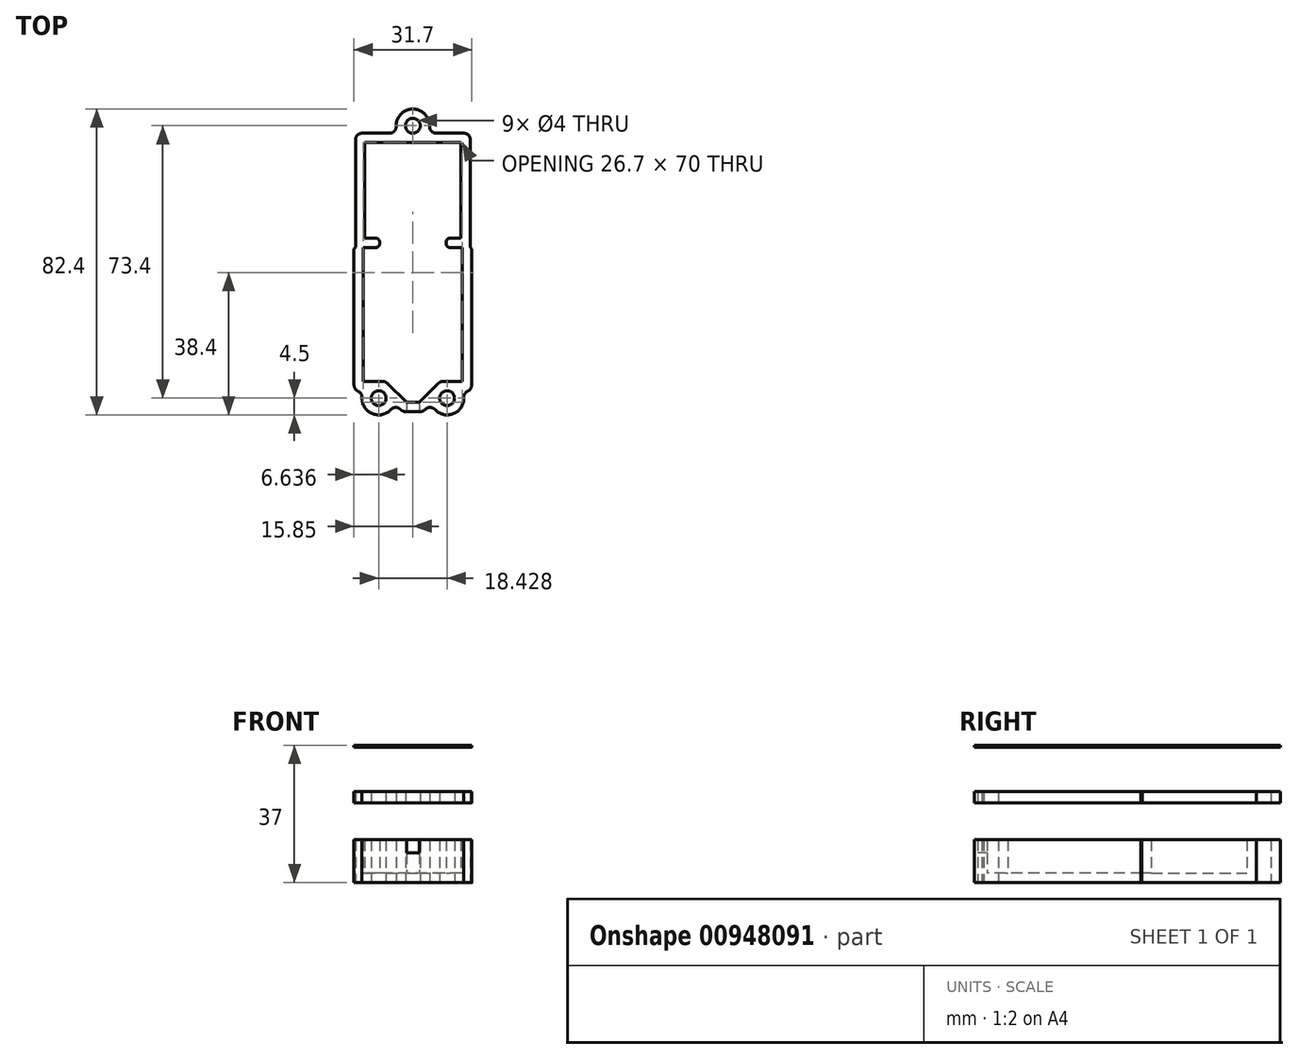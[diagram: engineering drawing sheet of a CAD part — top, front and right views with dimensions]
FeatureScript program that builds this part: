
annotation { "Feature Type Name" : "Feature", "Feature Type Description" : "" }
export const myFeature = defineFeature(function(context is Context, id is Id, definition is map)
    precondition{}
    {
        {
            var Q0;
            Q0=qCreatedBy(makeId("Top.planeOp"),FACE);
            var sketch = newSketch(context, id + "F0", { "sketchPlane" : qUnion([Q0])});
            skLineSegment(sketch, "E0.bottom", {"start": v(12.95, -12.9) * mm, "end": v(8.95, -12.9) * mm});
            skLineSegment(sketch, "E0.top", {"start": v(12.95, 12.9) * mm, "end": v(-12.95, 12.9) * mm});
            skLineSegment(sketch, "E0.left", {"start": v(12.95, -12.9) * mm, "end": v(12.95, 12.9) * mm});
            skLineSegment(sketch, "E0.right", {"start": v(-12.95, -12.9) * mm, "end": v(-12.95, 12.9) * mm});
            skPoint(sketch, "E0.middle", {"position": v(0, 0) * mm});
            skLineSegment(sketch, "E1.bottom", {"start": v(15.45, -15.4) * mm, "end": v(8.95, -15.4) * mm});
            skLineSegment(sketch, "E1.top", {"start": v(15.45, 15.4) * mm, "end": v(4.03, 15.4) * mm});
            skLineSegment(sketch, "E1.left", {"start": v(15.45, -15.4) * mm, "end": v(15.45, 15.4) * mm});
            skLineSegment(sketch, "E1.right", {"start": v(-15.45, -15.4) * mm, "end": v(-15.45, 15.4) * mm});
            skArc(sketch, "E2", {"start": v(4.03, 15.4) * mm, "mid": v(0, 21.9) * mm, "end": v(-4.03, 15.4) * mm});
            skCircle(sketch, "E3", {"center": v(0, 17.4) * mm, "radius": 2 * mm});
            skLineSegment(sketch, "E4.trimOffspring", {"start": v(-4.03, 15.4) * mm, "end": v(-15.45, 15.4) * mm});
            skLineSegment(sketch, "E5.bottom", {"start": v(13.35, -15.4) * mm, "end": v(8.95, -15.4) * mm});
            skLineSegment(sketch, "E5.top", {"start": v(13.35, -51.5) * mm, "end": v(7.35, -51.5) * mm});
            skLineSegment(sketch, "E5.left", {"start": v(13.35, -15.4) * mm, "end": v(13.35, -51.5) * mm});
            skLineSegment(sketch, "E5.right", {"start": v(-13.35, -15.4) * mm, "end": v(-13.35, -51.5) * mm});
            skPoint(sketch, "E5.middle", {"position": v(0, -33.45) * mm});
            skLineSegment(sketch, "E6.bottom", {"start": v(-15.85, -15.4) * mm, "end": v(-8.95, -15.4) * mm});
            skLineSegment(sketch, "E6.top", {"start": v(-15.85, -54) * mm, "end": v(-13.25, -54) * mm});
            skLineSegment(sketch, "E6.left", {"start": v(-15.85, -15.4) * mm, "end": v(-15.85, -54) * mm});
            skLineSegment(sketch, "E6.right", {"start": v(15.85, -15.4) * mm, "end": v(15.85, -54) * mm});
            skLineSegment(sketch, "E7", {"start": v(-8.95, -12.9) * mm, "end": v(-8.95, -15.4) * mm});
            skLineSegment(sketch, "E8", {"start": v(8.95, -12.9) * mm, "end": v(8.95, -15.4) * mm});
            skLineSegment(sketch, "E9.trimOffspring", {"start": v(-8.95, -12.9) * mm, "end": v(-12.95, -12.9) * mm});
            skLineSegment(sketch, "E10.trimOffspring", {"start": v(8.95, -15.4) * mm, "end": v(15.85, -15.4) * mm});
            skLineSegment(sketch, "E11.trimOffspring", {"start": v(-8.95, -15.4) * mm, "end": v(-13.35, -15.4) * mm});
            skLineSegment(sketch, "E12.trimOffspring", {"start": v(-8.95, -15.4) * mm, "end": v(-15.45, -15.4) * mm});
            skLineSegment(sketch, "E13", {"start": v(-7.35, -51.5) * mm, "end": v(-1.75, -57.1) * mm});
            skLineSegment(sketch, "E14", {"start": v(-1.75, -57.1) * mm, "end": v(1.75, -57.1) * mm});
            skLineSegment(sketch, "E15", {"start": v(1.75, -57.1) * mm, "end": v(7.35, -51.5) * mm});
            skPoint(sketch, "E16", {"position": v(-7.35, -51.5) * mm});
            skPoint(sketch, "E17", {"position": v(7.35, -51.5) * mm});
            skLineSegment(sketch, "E18.trimOffspring", {"start": v(-7.35, -51.5) * mm, "end": v(-13.35, -51.5) * mm});
            skLineSegment(sketch, "E19.trimOffspring", {"start": v(13.25, -54) * mm, "end": v(15.85, -54) * mm});
            skLineSegment(sketch, "E20", {"start": v(-4.95, -57.44) * mm, "end": v(-2.79, -59.6) * mm});
            skLineSegment(sketch, "E21", {"start": v(-2.79, -59.6) * mm, "end": v(2.79, -59.6) * mm});
            skLineSegment(sketch, "E22", {"start": v(2.79, -59.6) * mm, "end": v(7.8, -54.59) * mm});
            skLineSegment(sketch, "E23", {"start": v(-1.75, -57.1) * mm, "end": v(-1.75, -59.6) * mm});
            skLineSegment(sketch, "E24", {"start": v(1.75, -57.1) * mm, "end": v(1.75, -59.6) * mm});
            skArc(sketch, "E25", {"start": v(-13.25, -54) * mm, "mid": v(-10.94, -60.16) * mm, "end": v(-4.95, -57.44) * mm});
            skCircle(sketch, "E26", {"center": v(-9.21, -56) * mm, "radius": 2 * mm});
            skLineSegment(sketch, "E27", {"start": v(0, -0.95) * mm, "end": v(0, -33.45) * mm, "construction": true});
            skArc(sketch, "E28.MirrorCS", {"start": v(13.25, -54) * mm, "mid": v(10.94, -60.16) * mm, "end": v(4.95, -57.44) * mm});
            skCircle(sketch, "E29.MirrorC", {"center": v(9.21, -56) * mm, "radius": 2 * mm});
            skSolve(sketch);
        }
        {
            var Q0;
            Q0=makeQuery(id+"F0.imprint","IMPRINT",FACE,{"disambiguationData":[TD([[makeQuery(id+"F0.imprint","IMPRINT",EDGE,{"derivedFrom":sQuery(id+"F0.wireOp",EDGE,"E0.bottom")}),-1.0]])]});
            extrude(context, id + "F1", {"entities" : qUnion([Q0]), "depth" : 2.5 * mm, "offsetDistance" : 25 * mm});
        }
        {
            var Q0;
            Q0=makeQuery(id+"F0.imprint","IMPRINT",FACE,{"disambiguationData":[TD([[makeQuery(id+"F0.imprint","IMPRINT",EDGE,{"derivedFrom":sQuery(id+"F0.wireOp",EDGE,"E0.bottom")}),1.0]])]});
            var Q1;
            {var subQ3=sQuery(id+"F0.wireOp",EDGE,"E5.right");Q1=makeQuery(id+"F0.imprint","IMPRINT",FACE,{"disambiguationData":[TD([[makeQuery(id+"F0.imprint","IMPRINT",EDGE,{"derivedFrom":subQ3}),-1.0]])]});}
            var Q2;
            Q2=makeQuery(id+"F0.imprint","IMPRINT",FACE,{"disambiguationData":[TD([[makeQuery(id+"F0.imprint","IMPRINT",EDGE,{"derivedFrom":sQuery(id+"F0.wireOp",EDGE,"E5.top")}),1.0]])]});
            extrude(context, id + "F2", {"entities" : qUnion([Q0, Q1, Q2]), "operationType" : NewBodyOperationType.ADD, "depth" : 11.5 * mm, "offsetDistance" : 25 * mm});
        }
        {
            var Q0;
            Q0=makeQuery(id+"F0.imprint","IMPRINT",FACE,{"disambiguationData":[TD([[makeQuery(id+"F0.imprint","IMPRINT",EDGE,{"derivedFrom":sQuery(id+"F0.wireOp",EDGE,"E14")}),-1.0]])]});
            extrude(context, id + "F3", {"entities" : qUnion([Q0]), "operationType" : NewBodyOperationType.ADD, "depth" : 8 * mm, "offsetDistance" : 25 * mm});
        }
        {
            var Q0;
            Q0=makeQuery(id+"F3.opExtrude","CAP_EDGE",EDGE,{"disambiguationData":[OSD([sQuery(id+"F0.wireOp",EDGE,"E23")])],"isStart":false});
            var Q1;
            Q1=makeQuery(id+"F3.opExtrude","CAP_EDGE",EDGE,{"disambiguationData":[OSD([sQuery(id+"F0.wireOp",EDGE,"E24")])],"isStart":false});
            var Q2;
            Q2=makeQuery(id+"F2.opExtrude","SWEPT_EDGE",EDGE,{"disambiguationData":[OSD([sQuery(id+"F0.wireOp",EDGE,"E6.top"),sQuery(id+"F0.wireOp",EDGE,"E25")])]});
            var Q3;
            Q3=makeQuery(id+"F2.opExtrude","SWEPT_EDGE",EDGE,{"disambiguationData":[OSD([sQuery(id+"F0.wireOp",EDGE,"E20"),sQuery(id+"F0.wireOp",EDGE,"E25")])]});
            var Q4;
            Q4=makeQuery(id+"F2.opExtrude","SWEPT_EDGE",EDGE,{"disambiguationData":[OSD([sQuery(id+"F0.wireOp",EDGE,"E22"),sQuery(id+"F0.wireOp",EDGE,"E28.MirrorCS")])]});
            var Q5;
            Q5=makeQuery(id+"F2.opExtrude","SWEPT_EDGE",EDGE,{"disambiguationData":[OSD([sQuery(id+"F0.wireOp",EDGE,"E19.trimOffspring"),sQuery(id+"F0.wireOp",EDGE,"E28.MirrorCS")])]});
            var Q6;
            Q6=makeQuery(id+"F2.opExtrude","SWEPT_EDGE",EDGE,{"disambiguationData":[OSD([sQuery(id+"F0.wireOp",EDGE,"E21"),sQuery(id+"F0.wireOp",EDGE,"E22")])]});
            var Q7;
            Q7=makeQuery(id+"F2.opExtrude","SWEPT_EDGE",EDGE,{"disambiguationData":[OSD([sQuery(id+"F0.wireOp",EDGE,"E20"),sQuery(id+"F0.wireOp",EDGE,"E21")])]});
            var Q8;
            Q8=makeQuery(id+"F2.opExtrude","SWEPT_EDGE",EDGE,{"disambiguationData":[OSD([sQuery(id+"F0.wireOp",EDGE,"E2"),sQuery(id+"F0.wireOp",EDGE,"E4.trimOffspring")])]});
            var Q9;
            Q9=makeQuery(id+"F2.opExtrude","SWEPT_EDGE",EDGE,{"disambiguationData":[OSD([sQuery(id+"F0.wireOp",EDGE,"E1.top"),sQuery(id+"F0.wireOp",EDGE,"E2")])]});
            var Q10;
            Q10=makeQuery(id+"F2.opExtrude","SWEPT_EDGE",EDGE,{"disambiguationData":[OSD([sQuery(id+"F0.wireOp",EDGE,"E1.top"),sQuery(id+"F0.wireOp",EDGE,"E1.left")])]});
            var Q11;
            Q11=makeQuery(id+"F2.opExtrude","SWEPT_EDGE",EDGE,{"disambiguationData":[OSD([sQuery(id+"F0.wireOp",EDGE,"E1.right"),sQuery(id+"F0.wireOp",EDGE,"E4.trimOffspring")])]});
            var Q12;
            Q12=makeQuery(id+"F2.opExtrude","SWEPT_EDGE",EDGE,{"disambiguationData":[OSD([sQuery(id+"F0.wireOp",EDGE,"E5.top"),sQuery(id+"F0.wireOp",EDGE,"E15")])]});
            var Q13;
            Q13=makeQuery(id+"F2.opExtrude","SWEPT_EDGE",EDGE,{"disambiguationData":[OSD([sQuery(id+"F0.wireOp",EDGE,"E13"),sQuery(id+"F0.wireOp",EDGE,"E18.trimOffspring")])]});
            fillet(context, id + "F4", {"entities" : qUnion([Q0, Q1, Q2, Q3, Q4, Q5, Q6, Q7, Q8, Q9, Q10, Q11, Q12, Q13]), "radius" : 1.75 * mm, "tangentPropagation" : true, "allowEdgeOverflow" : false});
        }
        {
            var Q0;
            Q0=makeQuery(id+"F2.opExtrude","SWEPT_EDGE",EDGE,{"disambiguationData":[OSD([sQuery(id+"F0.wireOp",EDGE,"E6.right"),sQuery(id+"F0.wireOp",EDGE,"E10.trimOffspring")])]});
            var Q1;
            Q1=makeQuery(id+"F2.opExtrude","SWEPT_EDGE",EDGE,{"disambiguationData":[OSD([sQuery(id+"F0.wireOp",EDGE,"E6.bottom"),sQuery(id+"F0.wireOp",EDGE,"E6.left")])]});
            chamfer(context, id + "F5", {"entities" : qUnion([Q0, Q1]), "width" : 0.35 * mm, "tangentPropagation" : true});
        }
        {
            var Q0;
            Q0=makeQuery(id+"F2.opExtrude","SWEPT_EDGE",EDGE,{"disambiguationData":[OSD([sQuery(id+"F0.wireOp",EDGE,"E6.top"),sQuery(id+"F0.wireOp",EDGE,"E6.left")])]});
            var Q1;
            Q1=makeQuery(id+"F2.opExtrude","SWEPT_EDGE",EDGE,{"disambiguationData":[OSD([sQuery(id+"F0.wireOp",EDGE,"E6.right"),sQuery(id+"F0.wireOp",EDGE,"E19.trimOffspring")])]});
            fillet(context, id + "F6", {"entities" : qUnion([Q0, Q1]), "radius" : 2 * mm, "tangentPropagation" : true, "allowEdgeOverflow" : false});
        }
        {
            var Q0;
            Q0=makeQuery(id+"F2.opExtrude","CAP_FACE",FACE,{"disambiguationData":[OSD([sQuery(id+"F0.wireOp",EDGE,"E0.bottom"),sQuery(id+"F0.wireOp",EDGE,"E0.top"),sQuery(id+"F0.wireOp",EDGE,"E0.left"),sQuery(id+"F0.wireOp",EDGE,"E0.right"),sQuery(id+"F0.wireOp",EDGE,"E1.top"),sQuery(id+"F0.wireOp",EDGE,"E1.left"),sQuery(id+"F0.wireOp",EDGE,"E1.right"),sQuery(id+"F0.wireOp",EDGE,"E2"),sQuery(id+"F0.wireOp",EDGE,"E3"),sQuery(id+"F0.wireOp",EDGE,"E4.trimOffspring"),sQuery(id+"F0.wireOp",EDGE,"E5.top"),sQuery(id+"F0.wireOp",EDGE,"E5.left"),sQuery(id+"F0.wireOp",EDGE,"E5.right"),sQuery(id+"F0.wireOp",EDGE,"E6.bottom"),sQuery(id+"F0.wireOp",EDGE,"E6.top"),sQuery(id+"F0.wireOp",EDGE,"E6.left"),sQuery(id+"F0.wireOp",EDGE,"E6.right"),sQuery(id+"F0.wireOp",EDGE,"E7"),sQuery(id+"F0.wireOp",EDGE,"E8"),sQuery(id+"F0.wireOp",EDGE,"E9.trimOffspring"),sQuery(id+"F0.wireOp",EDGE,"E10.trimOffspring"),sQuery(id+"F0.wireOp",EDGE,"E12.trimOffspring"),sQuery(id+"F0.wireOp",EDGE,"E13"),sQuery(id+"F0.wireOp",EDGE,"E15"),sQuery(id+"F0.wireOp",EDGE,"E18.trimOffspring"),sQuery(id+"F0.wireOp",EDGE,"E19.trimOffspring"),sQuery(id+"F0.wireOp",EDGE,"E20"),sQuery(id+"F0.wireOp",EDGE,"E21"),sQuery(id+"F0.wireOp",EDGE,"E22"),sQuery(id+"F0.wireOp",EDGE,"E23"),sQuery(id+"F0.wireOp",EDGE,"E24"),sQuery(id+"F0.wireOp",EDGE,"E25"),sQuery(id+"F0.wireOp",EDGE,"E26"),sQuery(id+"F0.wireOp",EDGE,"E28.MirrorCS"),sQuery(id+"F0.wireOp",EDGE,"E29.MirrorC")])],"isStart":false});
            cPlane(context, id + "F7", {"entities" : qUnion([Q0]), "cplaneType" : CPlaneType.OFFSET, "offset" : 10 * mm, "width" : 150 * mm, "height" : 150 * mm});
        }
        {
            var Q0;
            Q0=qCreatedBy(id+"F7.planeOp",FACE);
            var sketch = newSketch(context, id + "F8", { "sketchPlane" : qUnion([Q0])});
            skLineSegment(sketch, "E30.0.0", {"start": v(-15.85, -15.75) * mm, "end": v(-15.85, -52.36) * mm});
            skArc(sketch, "E30.0.1", {"start": v(-15.85, -52.36) * mm, "mid": v(-15.54, -53.43) * mm, "end": v(-14.7, -54.17) * mm});
            skArc(sketch, "E30.0.2", {"start": v(-14.7, -54.17) * mm, "mid": v(-13.96, -54.84) * mm, "end": v(-13.71, -55.82) * mm});
            skArc(sketch, "E30.0.3", {"start": v(-13.71, -55.82) * mm, "mid": v(-10.94, -60.16) * mm, "end": v(-5.9, -59.05) * mm});
            skArc(sketch, "E30.0.4", {"start": v(-5.9, -59.05) * mm, "mid": v(-4.66, -58.49) * mm, "end": v(-3.38, -59) * mm});
            skLineSegment(sketch, "E30.0.5", {"start": v(-3.38, -59) * mm, "end": v(-3.3, -59.09) * mm});
            skArc(sketch, "E30.0.6", {"start": v(-3.3, -59.09) * mm, "mid": v(-2.73, -59.47) * mm, "end": v(-2.06, -59.6) * mm});
            skLineSegment(sketch, "E30.0.7", {"start": v(-2.06, -59.6) * mm, "end": v(-1.75, -59.6) * mm});
            skLineSegment(sketch, "E30.0.27", {"start": v(1.75, -59.6) * mm, "end": v(2.06, -59.6) * mm});
            skArc(sketch, "E30.0.28", {"start": v(2.06, -59.6) * mm, "mid": v(2.73, -59.47) * mm, "end": v(3.3, -59.09) * mm});
            skLineSegment(sketch, "E30.0.29", {"start": v(3.3, -59.09) * mm, "end": v(3.38, -59) * mm});
            skArc(sketch, "E30.0.30", {"start": v(3.38, -59) * mm, "mid": v(4.66, -58.49) * mm, "end": v(5.9, -59.05) * mm});
            skArc(sketch, "E30.0.31", {"start": v(5.9, -59.05) * mm, "mid": v(10.94, -60.16) * mm, "end": v(13.71, -55.82) * mm});
            skArc(sketch, "E30.0.32", {"start": v(13.71, -55.82) * mm, "mid": v(13.96, -54.84) * mm, "end": v(14.7, -54.17) * mm});
            skArc(sketch, "E30.0.33", {"start": v(14.7, -54.17) * mm, "mid": v(15.54, -53.43) * mm, "end": v(15.85, -52.36) * mm});
            skLineSegment(sketch, "E30.0.34", {"start": v(15.85, -52.36) * mm, "end": v(15.85, -15.75) * mm});
            skLineSegment(sketch, "E30.0.35", {"start": v(15.85, -15.75) * mm, "end": v(15.45, -15.35) * mm});
            skLineSegment(sketch, "E30.0.36", {"start": v(15.45, -15.35) * mm, "end": v(15.45, 13.65) * mm});
            skArc(sketch, "E30.0.37", {"start": v(15.45, 13.65) * mm, "mid": v(14.94, 14.89) * mm, "end": v(13.7, 15.4) * mm});
            skLineSegment(sketch, "E30.0.38", {"start": v(13.7, 15.4) * mm, "end": v(6.24, 15.4) * mm});
            skArc(sketch, "E30.0.39", {"start": v(6.24, 15.4) * mm, "mid": v(4.98, 15.94) * mm, "end": v(4.5, 17.22) * mm});
            skArc(sketch, "E30.0.40", {"start": v(4.5, 17.22) * mm, "mid": v(0, 21.9) * mm, "end": v(-4.5, 17.22) * mm});
            skArc(sketch, "E30.0.41", {"start": v(-4.5, 17.22) * mm, "mid": v(-4.98, 15.94) * mm, "end": v(-6.24, 15.4) * mm});
            skLineSegment(sketch, "E30.0.42", {"start": v(-6.24, 15.4) * mm, "end": v(-13.7, 15.4) * mm});
            skArc(sketch, "E30.0.43", {"start": v(-13.7, 15.4) * mm, "mid": v(-14.94, 14.89) * mm, "end": v(-15.45, 13.65) * mm});
            skLineSegment(sketch, "E30.0.44", {"start": v(-15.45, 13.65) * mm, "end": v(-15.45, -15.35) * mm});
            skLineSegment(sketch, "E30.0.45", {"start": v(-15.45, -15.35) * mm, "end": v(-15.85, -15.75) * mm});
            skPoint(sketch, "E30.0.17.end.orphan", {"position": v(12.95, 12.9) * mm});
            skPoint(sketch, "E30.0.17.start.orphan", {"position": v(-12.95, 12.9) * mm});
            skPoint(sketch, "E30.0.19.end.orphan", {"position": v(8.95, -12.9) * mm});
            skPoint(sketch, "E30.0.19.start.orphan", {"position": v(12.95, -12.9) * mm});
            skPoint(sketch, "E30.0.21.end.orphan", {"position": v(13.35, -15.4) * mm});
            skPoint(sketch, "E30.0.21.start.orphan", {"position": v(8.95, -15.4) * mm});
            skPoint(sketch, "E30.0.15.end.orphan", {"position": v(-12.95, -12.9) * mm});
            skPoint(sketch, "E30.0.15.start.orphan", {"position": v(-8.95, -12.9) * mm});
            skPoint(sketch, "E30.0.13.end.orphan", {"position": v(-8.95, -15.4) * mm});
            skPoint(sketch, "E30.0.13.start.orphan", {"position": v(-13.35, -15.4) * mm});
            skPoint(sketch, "E30.0.23.start.orphan", {"position": v(13.35, -51.5) * mm});
            skLineSegment(sketch, "E31", {"start": v(1.75, -59.6) * mm, "end": v(-1.75, -59.6) * mm});
            skPoint(sketch, "E30.0.10.start.orphan", {"position": v(-6.84, -52.01) * mm});
            skPoint(sketch, "E30.0.8.end.orphan", {"position": v(-1.75, -57.1) * mm});
            skPoint(sketch, "E30.0.26.start.orphan", {"position": v(1.75, -57.1) * mm});
            skPoint(sketch, "E30.0.24.end.orphan", {"position": v(6.84, -52.01) * mm});
            skPoint(sketch, "E30.0.24.start.orphan", {"position": v(8.07, -51.5) * mm});
            skPoint(sketch, "E30.0.11.end.orphan", {"position": v(-13.35, -51.5) * mm});
            skPoint(sketch, "E30.0.11.start.orphan", {"position": v(-8.07, -51.5) * mm});
            skCircle(sketch, "E32.0", {"center": v(9.21, -56) * mm, "radius": 2 * mm});
            skCircle(sketch, "E33.0", {"center": v(-9.21, -56) * mm, "radius": 2 * mm});
            skCircle(sketch, "E34.0", {"center": v(0, 17.4) * mm, "radius": 2 * mm});
            skSolve(sketch);
        }
        {
            var Q0;
            Q0=makeQuery(id+"F8.imprint","IMPRINT",FACE,{"disambiguationData":[TD([[makeQuery(id+"F8.imprint","IMPRINT",EDGE,{"derivedFrom":sQuery(id+"F8.wireOp",EDGE,"E30.0.0")}),1.0]])]});
            extrude(context, id + "F9", {"entities" : qUnion([Q0]), "depth" : 3 * mm, "offsetDistance" : 25 * mm});
        }
        {
            var Q0;
            Q0=makeQuery(id+"F2.opExtrude","SWEPT_EDGE",EDGE,{"disambiguationData":[OSD([sQuery(id+"F0.wireOp",EDGE,"E7"),sQuery(id+"F0.wireOp",EDGE,"E12.trimOffspring")])]});
            var Q1;
            Q1=makeQuery(id+"F2.opExtrude","SWEPT_EDGE",EDGE,{"disambiguationData":[OSD([sQuery(id+"F0.wireOp",EDGE,"E8"),sQuery(id+"F0.wireOp",EDGE,"E10.trimOffspring")])]});
            var Q2;
            Q2=makeQuery(id+"F2.opExtrude","SWEPT_EDGE",EDGE,{"disambiguationData":[OSD([sQuery(id+"F0.wireOp",EDGE,"E7"),sQuery(id+"F0.wireOp",EDGE,"E9.trimOffspring")])]});
            var Q3;
            Q3=makeQuery(id+"F2.opExtrude","SWEPT_EDGE",EDGE,{"disambiguationData":[OSD([sQuery(id+"F0.wireOp",EDGE,"E0.bottom"),sQuery(id+"F0.wireOp",EDGE,"E8")])]});
            fillet(context, id + "F10", {"entities" : qUnion([Q0, Q1, Q2, Q3]), "radius" : 1 * mm, "tangentPropagation" : true, "allowEdgeOverflow" : false});
        }
        {
            var Q0;
            Q0=makeQuery(id+"F2.opExtrude","CAP_FACE",FACE,{"disambiguationData":[OSD([sQuery(id+"F0.wireOp",EDGE,"E0.bottom"),sQuery(id+"F0.wireOp",EDGE,"E0.top"),sQuery(id+"F0.wireOp",EDGE,"E0.left"),sQuery(id+"F0.wireOp",EDGE,"E0.right"),sQuery(id+"F0.wireOp",EDGE,"E1.top"),sQuery(id+"F0.wireOp",EDGE,"E1.left"),sQuery(id+"F0.wireOp",EDGE,"E1.right"),sQuery(id+"F0.wireOp",EDGE,"E2"),sQuery(id+"F0.wireOp",EDGE,"E3"),sQuery(id+"F0.wireOp",EDGE,"E4.trimOffspring"),sQuery(id+"F0.wireOp",EDGE,"E5.top"),sQuery(id+"F0.wireOp",EDGE,"E5.left"),sQuery(id+"F0.wireOp",EDGE,"E5.right"),sQuery(id+"F0.wireOp",EDGE,"E6.bottom"),sQuery(id+"F0.wireOp",EDGE,"E6.top"),sQuery(id+"F0.wireOp",EDGE,"E6.left"),sQuery(id+"F0.wireOp",EDGE,"E6.right"),sQuery(id+"F0.wireOp",EDGE,"E7"),sQuery(id+"F0.wireOp",EDGE,"E8"),sQuery(id+"F0.wireOp",EDGE,"E9.trimOffspring"),sQuery(id+"F0.wireOp",EDGE,"E10.trimOffspring"),sQuery(id+"F0.wireOp",EDGE,"E12.trimOffspring"),sQuery(id+"F0.wireOp",EDGE,"E13"),sQuery(id+"F0.wireOp",EDGE,"E15"),sQuery(id+"F0.wireOp",EDGE,"E18.trimOffspring"),sQuery(id+"F0.wireOp",EDGE,"E19.trimOffspring"),sQuery(id+"F0.wireOp",EDGE,"E20"),sQuery(id+"F0.wireOp",EDGE,"E21"),sQuery(id+"F0.wireOp",EDGE,"E22"),sQuery(id+"F0.wireOp",EDGE,"E23"),sQuery(id+"F0.wireOp",EDGE,"E24"),sQuery(id+"F0.wireOp",EDGE,"E25"),sQuery(id+"F0.wireOp",EDGE,"E26"),sQuery(id+"F0.wireOp",EDGE,"E28.MirrorCS"),sQuery(id+"F0.wireOp",EDGE,"E29.MirrorC")])],"isStart":false});
            cPlane(context, id + "F11", {"entities" : qUnion([Q0]), "cplaneType" : CPlaneType.OFFSET, "offset" : 25 * mm, "width" : 150 * mm, "height" : 150 * mm});
        }
        {
            var Q0;
            Q0=qCreatedBy(id+"F11.planeOp",FACE);
            var sketch = newSketch(context, id + "F12", { "sketchPlane" : qUnion([Q0])});
            skLineSegment(sketch, "E35.0.0", {"start": v(-13.35, -15.4) * mm, "end": v(-9.95, -15.4) * mm});
            skArc(sketch, "E35.0.1", {"start": v(-9.95, -15.4) * mm, "mid": v(-9.24, -15.1) * mm, "end": v(-8.95, -14.4) * mm});
            skLineSegment(sketch, "E35.0.2", {"start": v(-8.95, -14.4) * mm, "end": v(-8.95, -13.9) * mm});
            skArc(sketch, "E35.0.3", {"start": v(-8.95, -13.9) * mm, "mid": v(-9.24, -13.2) * mm, "end": v(-9.95, -12.9) * mm});
            skLineSegment(sketch, "E35.0.4", {"start": v(-9.95, -12.9) * mm, "end": v(-12.95, -12.9) * mm});
            skLineSegment(sketch, "E35.0.5", {"start": v(-12.95, -12.9) * mm, "end": v(-12.95, 12.9) * mm});
            skLineSegment(sketch, "E35.0.6", {"start": v(-12.95, 12.9) * mm, "end": v(12.95, 12.9) * mm});
            skLineSegment(sketch, "E35.0.7", {"start": v(12.95, 12.9) * mm, "end": v(12.95, -12.9) * mm});
            skLineSegment(sketch, "E35.0.8", {"start": v(12.95, -12.9) * mm, "end": v(9.95, -12.9) * mm});
            skArc(sketch, "E35.0.9", {"start": v(9.95, -12.9) * mm, "mid": v(9.24, -13.2) * mm, "end": v(8.95, -13.9) * mm});
            skLineSegment(sketch, "E35.0.10", {"start": v(8.95, -13.9) * mm, "end": v(8.95, -14.4) * mm});
            skArc(sketch, "E35.0.11", {"start": v(8.95, -14.4) * mm, "mid": v(9.24, -15.1) * mm, "end": v(9.95, -15.4) * mm});
            skLineSegment(sketch, "E35.0.12", {"start": v(9.95, -15.4) * mm, "end": v(13.35, -15.4) * mm});
            skLineSegment(sketch, "E35.0.13", {"start": v(13.35, -15.4) * mm, "end": v(13.35, -51.5) * mm});
            skLineSegment(sketch, "E35.0.14", {"start": v(13.35, -51.5) * mm, "end": v(8.07, -51.5) * mm});
            skArc(sketch, "E35.0.15", {"start": v(8.07, -51.5) * mm, "mid": v(7.4, -51.63) * mm, "end": v(6.84, -52.01) * mm});
            skLineSegment(sketch, "E35.0.16", {"start": v(6.84, -52.01) * mm, "end": v(1.75, -57.1) * mm});
            skLineSegment(sketch, "E35.0.18", {"start": v(1.75, -59.6) * mm, "end": v(2.06, -59.6) * mm});
            skArc(sketch, "E35.0.19", {"start": v(2.06, -59.6) * mm, "mid": v(2.73, -59.47) * mm, "end": v(3.3, -59.09) * mm});
            skLineSegment(sketch, "E35.0.20", {"start": v(3.3, -59.09) * mm, "end": v(3.38, -59) * mm});
            skArc(sketch, "E35.0.21", {"start": v(3.38, -59) * mm, "mid": v(4.66, -58.49) * mm, "end": v(5.9, -59.05) * mm});
            skArc(sketch, "E35.0.22", {"start": v(5.9, -59.05) * mm, "mid": v(10.94, -60.16) * mm, "end": v(13.71, -55.82) * mm});
            skArc(sketch, "E35.0.23", {"start": v(13.71, -55.82) * mm, "mid": v(13.96, -54.84) * mm, "end": v(14.7, -54.17) * mm});
            skArc(sketch, "E35.0.24", {"start": v(14.7, -54.17) * mm, "mid": v(15.54, -53.43) * mm, "end": v(15.85, -52.36) * mm});
            skLineSegment(sketch, "E35.0.25", {"start": v(15.85, -52.36) * mm, "end": v(15.85, -15.75) * mm});
            skLineSegment(sketch, "E35.0.26", {"start": v(15.85, -15.75) * mm, "end": v(15.45, -15.35) * mm});
            skLineSegment(sketch, "E35.0.27", {"start": v(15.45, -15.35) * mm, "end": v(15.45, 13.65) * mm});
            skArc(sketch, "E35.0.28", {"start": v(15.45, 13.65) * mm, "mid": v(14.94, 14.89) * mm, "end": v(13.7, 15.4) * mm});
            skLineSegment(sketch, "E35.0.29", {"start": v(13.7, 15.4) * mm, "end": v(6.24, 15.4) * mm});
            skArc(sketch, "E35.0.30", {"start": v(6.24, 15.4) * mm, "mid": v(4.98, 15.94) * mm, "end": v(4.5, 17.22) * mm});
            skArc(sketch, "E35.0.31", {"start": v(4.5, 17.22) * mm, "mid": v(0, 21.9) * mm, "end": v(-4.5, 17.22) * mm});
            skArc(sketch, "E35.0.32", {"start": v(-4.5, 17.22) * mm, "mid": v(-4.98, 15.94) * mm, "end": v(-6.24, 15.4) * mm});
            skLineSegment(sketch, "E35.0.33", {"start": v(-6.24, 15.4) * mm, "end": v(-13.7, 15.4) * mm});
            skArc(sketch, "E35.0.34", {"start": v(-13.7, 15.4) * mm, "mid": v(-14.94, 14.89) * mm, "end": v(-15.45, 13.65) * mm});
            skLineSegment(sketch, "E35.0.35", {"start": v(-15.45, 13.65) * mm, "end": v(-15.45, -15.35) * mm});
            skLineSegment(sketch, "E35.0.36", {"start": v(-15.45, -15.35) * mm, "end": v(-15.85, -15.75) * mm});
            skLineSegment(sketch, "E35.0.37", {"start": v(-15.85, -15.75) * mm, "end": v(-15.85, -52.36) * mm});
            skArc(sketch, "E35.0.38", {"start": v(-15.85, -52.36) * mm, "mid": v(-15.54, -53.43) * mm, "end": v(-14.7, -54.17) * mm});
            skArc(sketch, "E35.0.39", {"start": v(-14.7, -54.17) * mm, "mid": v(-13.96, -54.84) * mm, "end": v(-13.71, -55.82) * mm});
            skArc(sketch, "E35.0.40", {"start": v(-13.71, -55.82) * mm, "mid": v(-10.94, -60.16) * mm, "end": v(-5.9, -59.05) * mm});
            skArc(sketch, "E35.0.41", {"start": v(-5.9, -59.05) * mm, "mid": v(-4.66, -58.49) * mm, "end": v(-3.38, -59) * mm});
            skLineSegment(sketch, "E35.0.42", {"start": v(-3.38, -59) * mm, "end": v(-3.3, -59.09) * mm});
            skArc(sketch, "E35.0.43", {"start": v(-3.3, -59.09) * mm, "mid": v(-2.73, -59.47) * mm, "end": v(-2.06, -59.6) * mm});
            skLineSegment(sketch, "E35.0.44", {"start": v(-2.06, -59.6) * mm, "end": v(-1.75, -59.6) * mm});
            skLineSegment(sketch, "E35.0.46", {"start": v(-1.75, -57.1) * mm, "end": v(-6.84, -52.01) * mm});
            skArc(sketch, "E35.0.47", {"start": v(-6.84, -52.01) * mm, "mid": v(-7.4, -51.63) * mm, "end": v(-8.07, -51.5) * mm});
            skLineSegment(sketch, "E35.0.48", {"start": v(-8.07, -51.5) * mm, "end": v(-13.35, -51.5) * mm});
            skLineSegment(sketch, "E35.0.49", {"start": v(-13.35, -51.5) * mm, "end": v(-13.35, -15.4) * mm});
            skCircle(sketch, "E36.0", {"center": v(-9.21, -56) * mm, "radius": 2 * mm});
            skCircle(sketch, "E37.0", {"center": v(9.21, -56) * mm, "radius": 2 * mm});
            skCircle(sketch, "E38.0", {"center": v(0, 17.4) * mm, "radius": 2 * mm});
            skLineSegment(sketch, "E39", {"start": v(-1.75, -57.1) * mm, "end": v(1.75, -57.1) * mm});
            skLineSegment(sketch, "E40", {"start": v(-1.75, -59.6) * mm, "end": v(1.75, -59.6) * mm});
            skSolve(sketch);
        }
        {
            var Q0;
            Q0=makeQuery(id+"F12.imprint","IMPRINT",FACE,{"disambiguationData":[TD([[makeQuery(id+"F12.imprint","IMPRINT",EDGE,{"derivedFrom":sQuery(id+"F12.wireOp",EDGE,"E35.0.0")}),1.0]])]});
            extrude(context, id + "F13", {"entities" : qUnion([Q0]), "depth" : 0.5 * mm, "offsetDistance" : 25 * mm});
        }
    });
